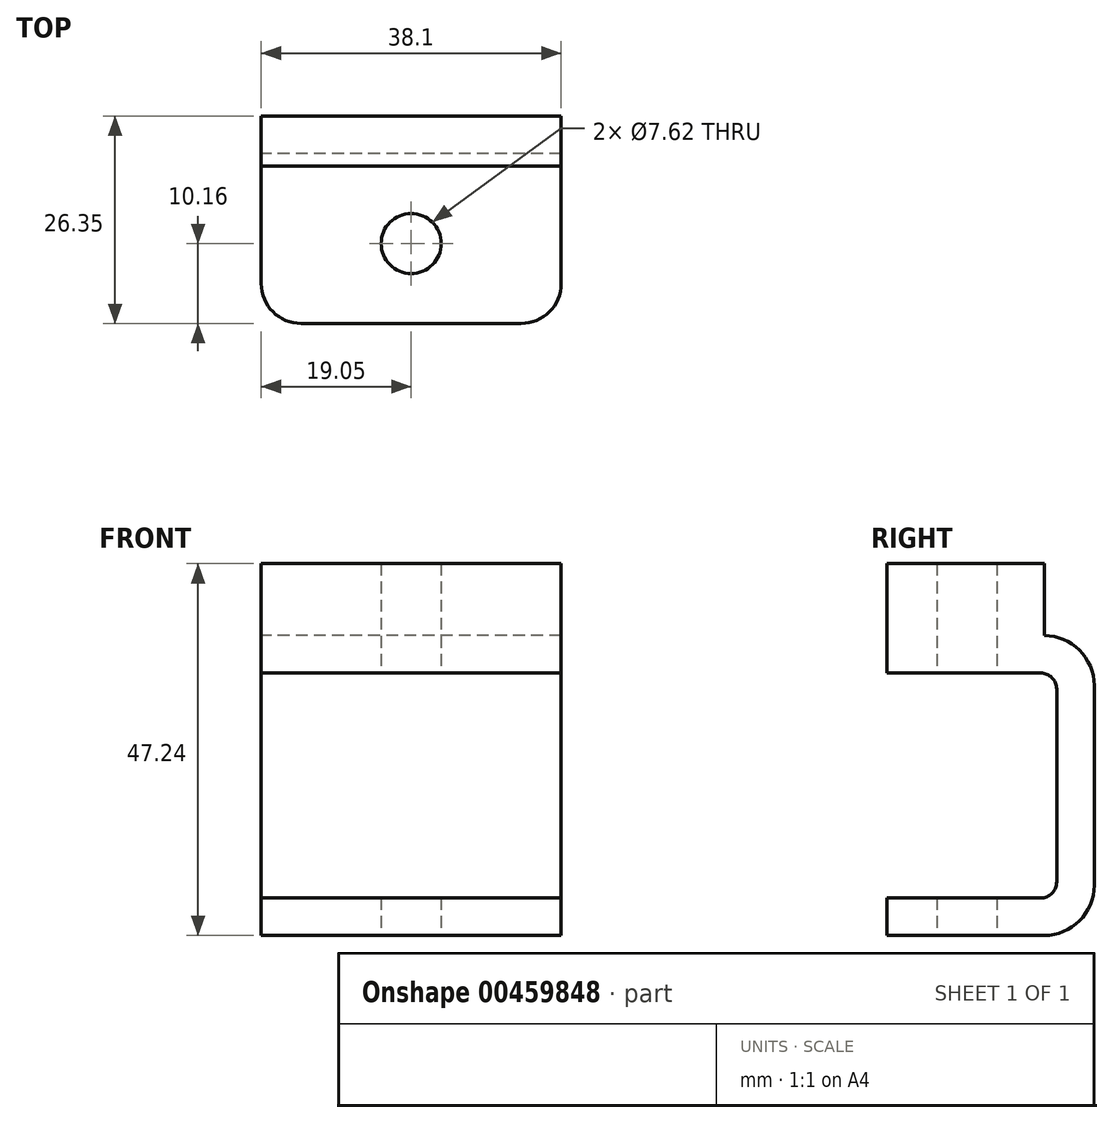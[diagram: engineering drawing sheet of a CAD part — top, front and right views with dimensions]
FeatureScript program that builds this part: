
annotation { "Feature Type Name" : "Feature", "Feature Type Description" : "" }
export const myFeature = defineFeature(function(context is Context, id is Id, definition is map)
    precondition{}
    {
        {
            var Q0;
            Q0=qCreatedBy(makeId("Right.planeOp"),FACE);
            var sketch = newSketch(context, id + "F0", { "sketchPlane" : qUnion([Q0])});
            skLineSegment(sketch, "E0.bottom", {"start": v(0, 0) * mm, "end": v(19.56, 0) * mm});
            skLineSegment(sketch, "E0.top", {"start": v(0, 28.57) * mm, "end": v(19.56, 28.57) * mm});
            skLineSegment(sketch, "E0.left", {"start": v(0, 0) * mm, "end": v(0, 28.57) * mm, "construction": true});
            skLineSegment(sketch, "E0.right", {"start": v(21.59, 2.03) * mm, "end": v(21.59, 26.54) * mm});
            skLineSegment(sketch, "E1.0", {"start": v(0, 33.34) * mm, "end": v(20, 33.34) * mm});
            skLineSegment(sketch, "E1.1", {"start": v(26.35, 1.59) * mm, "end": v(26.35, 26.99) * mm});
            skLineSegment(sketch, "E1.2", {"start": v(0, -4.76) * mm, "end": v(20, -4.76) * mm});
            skLineSegment(sketch, "E2", {"start": v(0, -4.76) * mm, "end": v(0, 0) * mm});
            skLineSegment(sketch, "E3", {"start": v(0, 28.57) * mm, "end": v(0, 33.34) * mm});
            skPoint(sketch, "E4.visualSharp", {"position": v(21.59, 28.57) * mm});
            skArc(sketch, "E4.filletArc", {"start": v(21.59, 26.54) * mm, "mid": v(21, 27.98) * mm, "end": v(19.56, 28.58) * mm});
            skPoint(sketch, "E5.visualSharp", {"position": v(21.59, 0) * mm});
            skArc(sketch, "E5.filletArc", {"start": v(19.56, 0) * mm, "mid": v(21, 0.6) * mm, "end": v(21.6, 2.03) * mm});
            skPoint(sketch, "E6.visualSharp", {"position": v(26.35, 33.34) * mm});
            skArc(sketch, "E6.filletArc", {"start": v(26.35, 26.99) * mm, "mid": v(24.5, 31.48) * mm, "end": v(20, 33.34) * mm});
            skPoint(sketch, "E7.visualSharp", {"position": v(26.35, -4.76) * mm});
            skArc(sketch, "E7.filletArc", {"start": v(20, -4.76) * mm, "mid": v(24.5, -2.9) * mm, "end": v(26.35, 1.59) * mm});
            skSolve(sketch);
        }
        {
            var Q0;
            Q0=qSketchRegion(id+"F0",true);
            extrude(context, id + "F1", {"entities" : qUnion([Q0]), "endBound" : BoundingType.SYMMETRIC, "depth" : 38.1 * mm});
        }
        {
            var Q0;
            Q0=makeQuery(id+"F1.opExtrude","SWEPT_FACE",FACE,{"disambiguationData":[OSD([sQuery(id+"F0.wireOp",EDGE,"E1.2")])]});
            var sketch = newSketch(context, id + "F2", { "sketchPlane" : qUnion([Q0])});
            skLineSegment(sketch, "E8", {"start": v(0, 0) * mm, "end": v(0, -26.35) * mm});
            skCircle(sketch, "E9", {"center": v(0, -10.16) * mm, "radius": 3.81 * mm});
            skSolve(sketch);
        }
        {
            var Q0;
            Q0=qSketchRegion(id+"F2",true);
            extrude(context, id + "F3", {"entities" : qUnion([Q0]), "operationType" : NewBodyOperationType.REMOVE, "oppositeDirection" : true, "depth" : 70.54 * mm});
        }
        {
            var Q0;
            Q0=makeQuery(id+"F1.opExtrude","CAP_EDGE",EDGE,{"disambiguationData":[OSD([sQuery(id+"F0.wireOp",EDGE,"E3")])],"isStart":true});
            var Q1;
            Q1=makeQuery(id+"F1.opExtrude","CAP_EDGE",EDGE,{"disambiguationData":[OSD([sQuery(id+"F0.wireOp",EDGE,"E3")])],"isStart":false});
            var Q2;
            Q2=makeQuery(id+"F1.opExtrude","CAP_EDGE",EDGE,{"disambiguationData":[OSD([sQuery(id+"F0.wireOp",EDGE,"E2")])],"isStart":false});
            var Q3;
            Q3=makeQuery(id+"F1.opExtrude","CAP_EDGE",EDGE,{"disambiguationData":[OSD([sQuery(id+"F0.wireOp",EDGE,"E2")])],"isStart":true});
            fillet(context, id + "F4", {"entities" : qUnion([Q0, Q1, Q2, Q3]), "radius" : 5.08 * mm, "tangentPropagation" : true, "allowEdgeOverflow" : false});
        }
        {
            var Q0;
            Q0=makeQuery(id+"F1.opExtrude","SWEPT_FACE",FACE,{"disambiguationData":[OSD([sQuery(id+"F0.wireOp",EDGE,"E1.0")])]});
            var sketch = newSketch(context, id + "F5", { "sketchPlane" : qUnion([Q0])});
            skSolve(sketch);
        }
        {
            var Q0;
            {var subQ0=sQuery(id+"F0.wireOp",EDGE,"E1.0");Q0=makeQuery(id+"F5.imprint","IMPRINT",FACE,{"disambiguationData":[TD([[makeQuery(id+"F5.imprint","IMPRINT",EDGE,{"derivedFrom":makeQuery(id+"F1.opExtrude","CAP_EDGE",EDGE,{"disambiguationData":[OSD([subQ0])],"isStart":true})}),-1.0]])]});}
            extrude(context, id + "F6", {"entities" : qUnion([Q0]), "operationType" : NewBodyOperationType.ADD, "depth" : 9.14 * mm});
        }
    });
